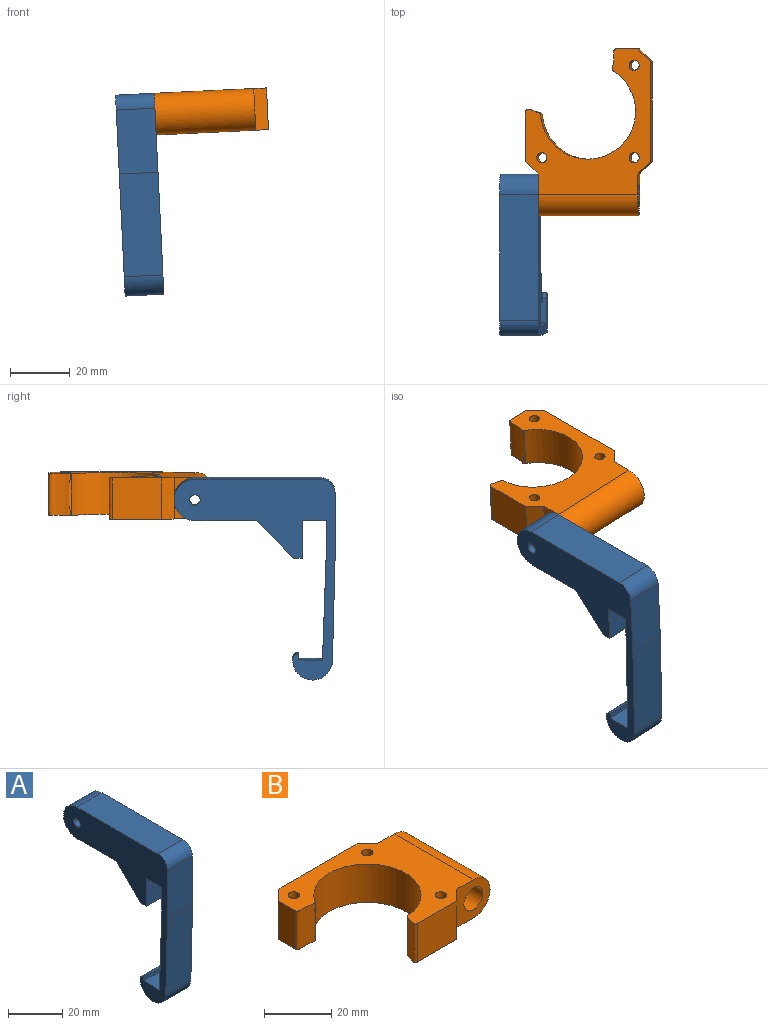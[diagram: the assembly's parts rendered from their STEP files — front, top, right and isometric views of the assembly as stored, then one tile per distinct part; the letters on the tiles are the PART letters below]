
ASSEMBLY  parts=2 mates=1
PART A: 21 faces, bbox 13x54x67.5 mm
  f0: plane 13x12.5mm, normal (0,0.71,-0.71), area 229.8mm2, adj f1,f15,f17,f18
  f1: plane 20.5x13mm, normal (0,0,-1), area 266.5mm2, adj f0,f2,f17,f18
  f2: cylinder r=7mm len=14mm, axis (-1,0,0), area 285.9mm2, adj f1,f3,f17,f18
  f3: plane 42x13mm, normal (0,0,1), area 546mm2, adj f2,f4,f17,f18
  f4: cylinder r=5mm len=13mm, axis (-1,0,0), area 102.1mm2, adj f3,f5,f17,f18
  f5: plane 21.5x13mm, normal (0,-1,0), area 279.5mm2, adj f4,f6,f17,f18
  f6: plane 34.49x13mm, normal (0,-1,-0.03), area 448.5mm2, adj f5,f7,f17,f18
  f7: cylinder r=6.67mm len=13.33mm, axis (-1,0,0), area 272.2mm2, adj f6,f8,f17,f18
  f8: cylinder r=2mm len=13mm, axis (-1,0,0), area 40.2mm2, adj f7,f9,f17,f18
  f9: plane 13x2mm, normal (0,-1,0), area 26mm2, adj f8,f10,f17,f18
  f10: plane 13x8mm, normal (0,-0.03,1), area 104mm2, adj f9,f11,f17,f18
  f11: plane 34.41x13mm, normal (0,1,0.03), area 447.5mm2, adj f10,f12,f17,f18
  f12: plane 13x12.5mm, normal (0,1,0), area 162.5mm2, adj f11,f13,f17,f18
  f13: plane 13x8mm, normal (0,0,-1), area 104mm2, adj f12,f14,f17,f18
  f14: plane 13x12.5mm, normal (0,-1,0), area 162.5mm2, adj f13,f15,f17,f18
  f15: plane 13x3mm, normal (0,0,-1), area 39mm2, adj f0,f14,f17,f18
  f16: cylinder r=4.1mm len=10mm, axis (-1,0,0), area 257.6mm2, adj f17,f20
  f17: plane 67.49x54mm, normal (1,0,0), area 1011.9mm2, adj f0,f1,f2,f3,f4,f5,f6,f7
  f18: plane 67.49x54mm, normal (-1,0,0), area 1055.1mm2, adj f0,f1,f2,f3,f4,f5,f6,f7
  f19: cylinder r=1.75mm len=3.5mm, axis (-1,0,0), area 33mm2, adj f18,f20
  f20: plane 8.2x8.2mm, normal (1,0,0), area 43.2mm2, adj f16,f19
PART B: 18 faces, bbox 56x42x14 mm
  f0: extruded ~14x5.04mm, area 85.3mm2, adj f1,f10,f12,f13
  f1: cylinder r=16mm len=31.96mm, axis (0,0,1), area 913.6mm2, adj f0,f2,f12,f13
  f2: extruded ~14x7.47mm, area 111.6mm2, adj f1,f3,f12,f13
  f3: plane 14x7.31mm, normal (-1,0,0), area 102.3mm2, adj f2,f4,f12,f13
  f4: plane 14x4.31mm, normal (-0.71,0.71,0), area 85.2mm2, adj f3,f5,f12,f13
  f5: plane 33.41x14mm, normal (0,1,0), area 467.7mm2, adj f4,f6,f12,f13
  f6: plane 14x4.3mm, normal (0.71,0.71,0), area 84.9mm2, adj f5,f12,f13,f15
  f7: plane 14x4.31mm, normal (0.71,-0.71,0), area 85.1mm2, adj f10,f12,f13,f14
  f8: cylinder r=1.7mm len=14mm, axis (0,0,1), area 149.5mm2, adj f12,f13
  f9: cylinder r=1.7mm len=14mm, axis (0,0,1), area 149.5mm2, adj f12,f13
  f10: plane 16.52x14mm, normal (0,-1,0), area 231.2mm2, adj f0,f7,f12,f13
  f11: cylinder r=1.7mm len=14mm, axis (0,0,1), area 149.5mm2, adj f12,f13
  f12: plane 49x42mm, normal (0,0,-1), area 849.7mm2, adj f0,f1,f2,f3,f4,f5,f6,f7
  f13: plane 49x42mm, normal (0,0,1), area 849.7mm2, adj f0,f1,f2,f3,f4,f5,f6,f7
  f14: plane 14x14mm, normal (0,-1,0), area 124.7mm2, adj f7,f12,f13,f16,f17
  f15: plane 14x14mm, normal (0,1,0), area 124.7mm2, adj f6,f12,f13,f16,f17
  f16: cylinder r=4mm len=33.41mm, axis (0,1,0), area 839.7mm2, adj f14,f15
  f17: cylinder r=7mm len=33.41mm, axis (0,-1,0), area 734.8mm2, adj f12,f13,f14,f15
PLACE A rot(axis=(0,-1,0),2.7deg) t=(-18.8,-76.22,-16.97)mm fixed
PLACE B rot(axis=(0.02,-0.02,-1),90deg) t=(-32.95,-1.22,21.4)mm
MATE revolute A.f2 <-> B.f17  axis (1,0,0.05) through (-7.35,-29.22,15.62)mm
